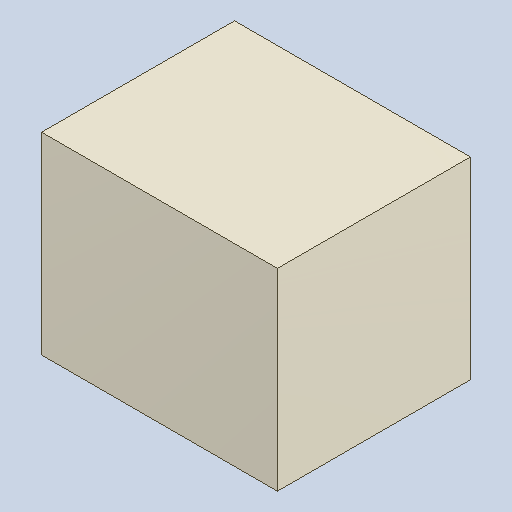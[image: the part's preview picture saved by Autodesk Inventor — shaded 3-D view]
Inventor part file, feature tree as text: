
AUTODESK INVENTOR PART (.ipt)
format: ipt  version: 2023.4 (Build 274418000, 418)  size: 81,920 bytes
history: native  units: mm
features: extrude x1
ambient origin geometry x8: Origin, YZ Plane, XZ Plane, XY Plane, X Axis, Y Axis, Z Axis, Center Point
bodies: Solid1 (feature_tree)
feature tree (1):
  extrude  "Extruded_12"  [1 undecoded]
note: 1 required parameter value undecoded (feature->parameter linkage not recoverable at this tier; creation-order binding heuristic only, values carry confidence <= 0.55)
